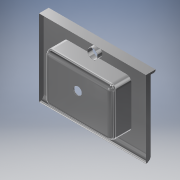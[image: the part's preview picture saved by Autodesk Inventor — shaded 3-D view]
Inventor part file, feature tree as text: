
AUTODESK INVENTOR PART (.ipt)
format: ipt  version: 2016 (Build 200138000, 138)  size: 368,640 bytes
history: native  units: mm
features: sketch x19, extrude x7, revolve x4, sweep x4, other x1, fillet x1, shell x1
ambient origin geometry x8: Origin, YZ Plane, XZ Plane, XY Plane, X Axis, Y Axis, Z Axis, Center Point
bodies: Body1 (feature_tree)
feature tree (37):
  other  "Sólido1"
  sketch  "Boceto1"  dims[d2=700.0mm d3=500.0mm]
  extrude  "Extrusión1"  Depth=500.0mm
  revolve  "Revolución1"  [1 undecoded]
  revolve  "Revolución2"  Angle=90.0deg
  revolve  "Revolución3"  Angle=90.0deg
  revolve  "Revolución4"  [1 undecoded]
  extrude  "Extrusión2"  TaperAngle=0.0deg  [1 undecoded]
  sweep  "Barrido1"
  sweep  "Barrido2"
  sweep  "Barrido3"
  sweep  "Barrido4"
  extrude  "Extrusión3"  Depth=50.0mm
  extrude  "Extrusión4"  Depth=50.0mm
  extrude  "Extrusión6"  Depth=20.0mm
  fillet  "Fillet1"  Radius=20.0mm
  extrude  "Extrusion11"  Depth=100.0mm
  extrude  "Extrusion12"  Depth=10.0mm TaperAngle=0.0deg
  shell  "Shell1"  Thickness=1.0mm
  sketch  "Boceto3"  dims[d13=90.0deg d14=90.0deg]
  sketch  "Boceto4"  dims[d18=0.0mm d19=0.0mm]
  sketch  "Boceto5"  dims[d22=80.0mm d23=10.0mm d24=0.0mm]
  sketch  "Boceto6"  dims[d25=100.0mm d26=3.0mm d27=0.0mm]
  sketch  "Boceto7"  dims[d29=0.0mm d30=0.0mm d31=0.0mm d32=0.0mm d41=700.0mm]
  sketch  "Boceto8"  dims[d42=500.0mm d43=50.0mm]
  sketch  "Boceto 3D1"  dims[d4=2.0mm d5=50.0mm]
  sketch  "Boceto9"  dims[d44=50.0mm d45=0.0mm d67=50.0mm]
  sketch  "Boceto 3D2"  dims[d10=150.0mm d11=0.0mm d12=90.0deg]
  sketch  "Boceto10"  dims[d71=101.6mm d72=255.0mm d73=20.0mm d74=0.0mm]
  sketch  "Boceto 3D3"  dims[d15=90.0deg d16=400.0mm d17=0.0mm]
  sketch  "Boceto11"  dims[d75=20.0mm d76=100.0mm]
  sketch  "Boceto 3D4"  dims[d20=0.0mm d21=0.0mm]
  sketch  "Boceto12"  dims[d77=20.0mm d78=10.0mm d79=0.0mm d80=1.0mm]
  sketch  "Boceto13"  dims[d81=200.0mm]
  sketch  "Boceto15"  dims[d82=350.0mm]
  sketch  "Sketch21"
  sketch  "Sketch22"
note: 3 required parameter values undecoded (feature->parameter linkage not recoverable at this tier; creation-order binding heuristic only, values carry confidence <= 0.55)